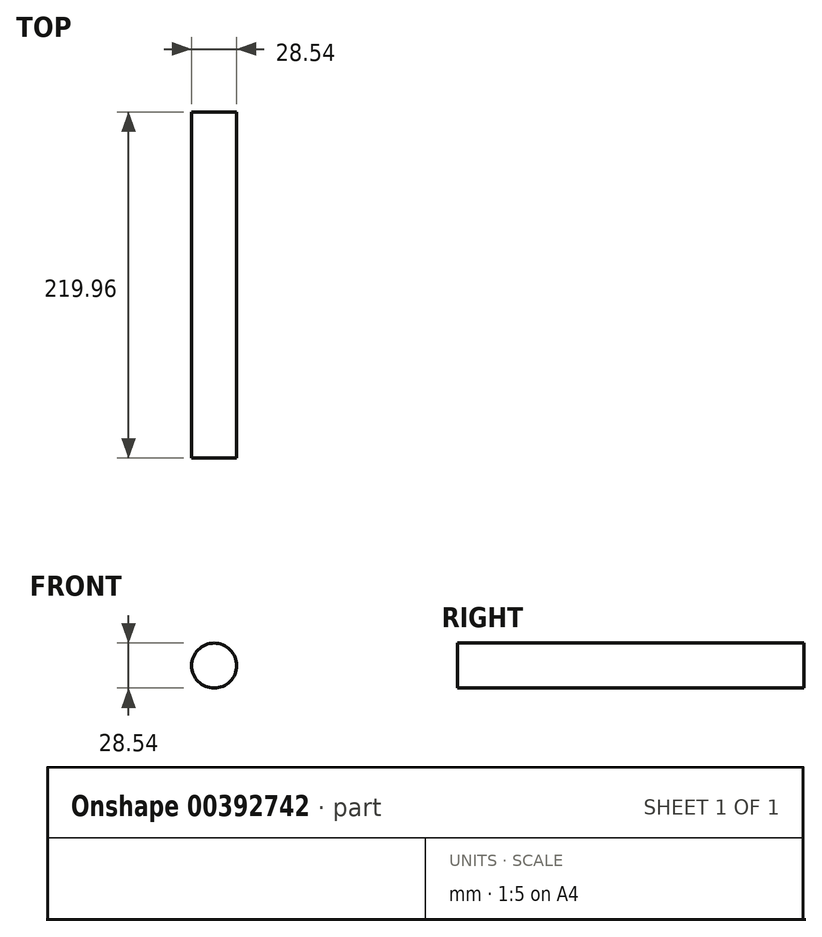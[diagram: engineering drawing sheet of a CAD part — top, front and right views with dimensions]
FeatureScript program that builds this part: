
annotation { "Feature Type Name" : "Feature", "Feature Type Description" : "" }
export const myFeature = defineFeature(function(context is Context, id is Id, definition is map)
    precondition{}
    {
        {
            var Q0;
            Q0=qCreatedBy(makeId("Front.planeOp"),FACE);
            var sketch = newSketch(context, id + "F0", { "sketchPlane" : qUnion([Q0])});
            skCircle(sketch, "E0", {"center": v(0, 0) * mm, "radius": 14.27 * mm});
            skSolve(sketch);
        }
        {
            var Q0;
            Q0 = qSketchRegion(id + "F0", true);
            extrude(context, id + "F1", {"entities" : qUnion([Q0]), "endBound" : BoundingType.SYMMETRIC, "depth" : 219.96 * mm});
        }
    });
